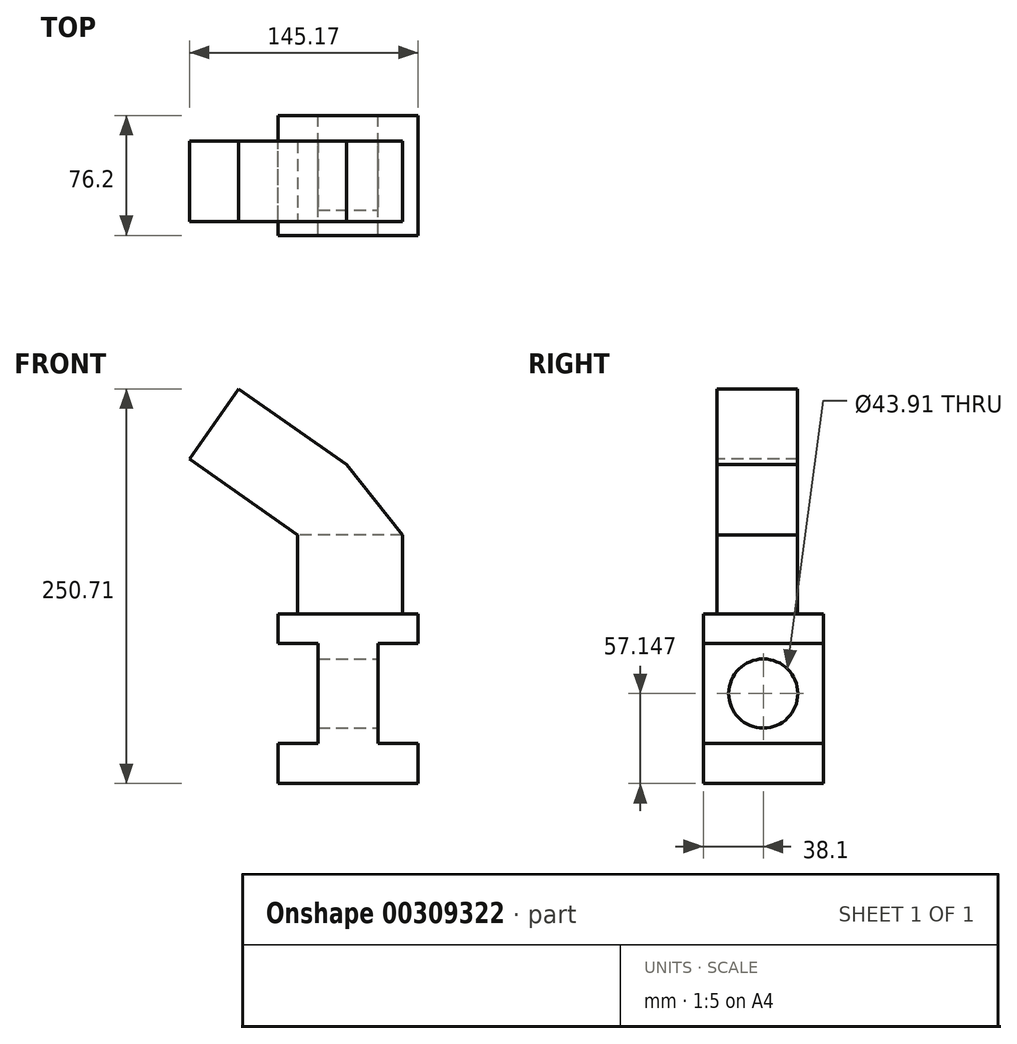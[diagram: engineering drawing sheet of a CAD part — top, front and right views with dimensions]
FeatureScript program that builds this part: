
annotation { "Feature Type Name" : "Feature", "Feature Type Description" : "" }
export const myFeature = defineFeature(function(context is Context, id is Id, definition is map)
    precondition{}
    {
        {
            var Q0;
            Q0=qCreatedBy(makeId("Front.planeOp"),FACE);
            var sketch = newSketch(context, id + "F0", { "sketchPlane" : qUnion([Q0])});
            skLineSegment(sketch, "E0", {"start": v(-43.68, -35.07) * mm, "end": v(45.22, -35.07) * mm});
            skLineSegment(sketch, "E1", {"start": v(45.22, -35.07) * mm, "end": v(45.22, -9.67) * mm});
            skLineSegment(sketch, "E2", {"start": v(45.22, -9.67) * mm, "end": v(19.82, -9.67) * mm});
            skLineSegment(sketch, "E3", {"start": v(19.82, -9.67) * mm, "end": v(19.82, 53.83) * mm});
            skLineSegment(sketch, "E4", {"start": v(19.82, 53.83) * mm, "end": v(45.22, 53.83) * mm});
            skLineSegment(sketch, "E5", {"start": v(45.22, 53.83) * mm, "end": v(45.22, 72.53) * mm});
            skLineSegment(sketch, "E6", {"start": v(45.22, 72.53) * mm, "end": v(-43.68, 72.53) * mm});
            skLineSegment(sketch, "E7", {"start": v(-43.68, 72.53) * mm, "end": v(-43.68, 53.83) * mm});
            skLineSegment(sketch, "E8", {"start": v(-43.68, 53.83) * mm, "end": v(-18.28, 53.83) * mm});
            skLineSegment(sketch, "E9", {"start": v(-18.28, 53.83) * mm, "end": v(-18.28, -9.67) * mm});
            skLineSegment(sketch, "E10", {"start": v(-18.28, -9.67) * mm, "end": v(-43.68, -9.67) * mm});
            skLineSegment(sketch, "E11", {"start": v(-43.68, -9.67) * mm, "end": v(-43.68, -35.07) * mm});
            skSolve(sketch);
        }
        {
            var Q0;
            Q0=makeQuery(id+"F0.imprint","IMPRINT",FACE,{"disambiguationData":[TD([[makeQuery(id+"F0.imprint","IMPRINT",EDGE,{"derivedFrom":sQuery(id+"F0.wireOp",EDGE,"E0")}),1.0]])]});
            extrude(context, id + "F1", {"entities" : qUnion([Q0]), "depth" : 76.2 * mm});
        }
        {
            var Q0;
            Q0=makeQuery(id+"F1.opExtrude","SWEPT_FACE",FACE,{"disambiguationData":[OSD([sQuery(id+"F0.wireOp",EDGE,"E3")])]});
            var sketch = newSketch(context, id + "F2", { "sketchPlane" : qUnion([Q0])});
            skCircle(sketch, "E12", {"center": v(-38.1, 22.08) * mm, "radius": 21.95 * mm});
            skPoint(sketch, "E12.centerSnap0", {"position": v(-38.1, 53.83) * mm});
            skPoint(sketch, "E12.centerSnap1", {"position": v(-76.2, 22.08) * mm});
            skSolve(sketch);
        }
        {
            var Q0;
            Q0=makeQuery(id+"F2.imprint","IMPRINT",FACE,{"disambiguationData":[TD([[makeQuery(id+"F2.imprint","IMPRINT",EDGE,{"derivedFrom":sQuery(id+"F2.wireOp",EDGE,"E12")}),1.0]])]});
            extrude(context, id + "F3", {"entities" : qUnion([Q0]), "operationType" : NewBodyOperationType.REMOVE, "endBound" : BoundingType.THROUGH_ALL, "oppositeDirection" : true, "depth" : 25.4 * mm});
        }
        {
            var Q0;
            Q0=makeQuery(id+"F1.opExtrude","SWEPT_FACE",FACE,{"disambiguationData":[OSD([sQuery(id+"F0.wireOp",EDGE,"E6")])]});
            var sketch = newSketch(context, id + "F4", { "sketchPlane" : qUnion([Q0])});
            skLineSegment(sketch, "E13", {"start": v(35.27, -16.41) * mm, "end": v(-31.35, -16.41) * mm});
            skLineSegment(sketch, "E14", {"start": v(-31.35, -16.41) * mm, "end": v(-31.35, -67.35) * mm});
            skLineSegment(sketch, "E15", {"start": v(-31.35, -67.35) * mm, "end": v(35.27, -67.35) * mm});
            skLineSegment(sketch, "E16", {"start": v(35.27, -67.35) * mm, "end": v(35.27, -16.41) * mm});
            skSolve(sketch);
        }
        {
            var Q0;
            Q0=makeQuery(id+"F4.imprint","IMPRINT",FACE,{"disambiguationData":[TD([[makeQuery(id+"F4.imprint","IMPRINT",EDGE,{"derivedFrom":sQuery(id+"F4.wireOp",EDGE,"E13")}),1.0]])]});
            extrude(context, id + "F5", {"entities" : qUnion([Q0]), "operationType" : NewBodyOperationType.ADD, "depth" : 50.3 * mm});
        }
        {
            var Q0;
            Q0=makeQuery(id+"F5.opExtrude","SWEPT_FACE",FACE,{"disambiguationData":[OSD([sQuery(id+"F4.wireOp",EDGE,"E15")])]});
            var sketch = newSketch(context, id + "F6", { "sketchPlane" : qUnion([Q0])});
            skLineSegment(sketch, "E17", {"start": v(-31.35, 122.82) * mm, "end": v(0, 167.47) * mm});
            skLineSegment(sketch, "E18", {"start": v(0, 167.47) * mm, "end": v(35.27, 122.82) * mm});
            skSolve(sketch);
        }
        {
            var Q0;
            Q0=makeQuery(id+"F6.imprint","IMPRINT",FACE,{"disambiguationData":[TD([[makeQuery(id+"F6.imprint","IMPRINT",EDGE,{"derivedFrom":sQuery(id+"F6.wireOp",EDGE,"E17")}),-1.0]])]});
            extrude(context, id + "F7", {"entities" : qUnion([Q0]), "operationType" : NewBodyOperationType.ADD, "oppositeDirection" : true, "depth" : 51.05 * mm});
        }
        {
            var Q0;
            {var subQ0=sQuery(id+"F4.wireOp",EDGE,"E15");Q0=makeQuery(id+"F7.boolean.opBoolean","MERGE",FACE,{"derivedFrom":[makeQuery(id+"F5.opExtrude","SWEPT_FACE",FACE,{"disambiguationData":[OSD([subQ0])]}),makeQuery(id+"F7.opExtrude","CAP_FACE",FACE,{"disambiguationData":[OSD([subQ0,sQuery(id+"F6.wireOp",EDGE,"E17"),sQuery(id+"F6.wireOp",EDGE,"E18")])],"isStart":true})]});}
            var sketch = newSketch(context, id + "F8", { "sketchPlane" : qUnion([Q0])});
            skPoint(sketch, "E19.oppositeSnap0", {"position": v(-31.35, 97.67) * mm});
            skLineSegment(sketch, "E19.bottom", {"start": v(-31.35, 97.67) * mm, "end": v(-11.19, 97.67) * mm});
            skLineSegment(sketch, "E19.top", {"start": v(-31.35, 97.67) * mm, "end": v(-11.19, 97.67) * mm});
            skLineSegment(sketch, "E19.left", {"start": v(-31.35, 97.67) * mm, "end": v(-31.35, 97.67) * mm});
            skLineSegment(sketch, "E19.right", {"start": v(-11.19, 97.67) * mm, "end": v(-11.19, 97.67) * mm});
            skLineSegment(sketch, "E20", {"start": v(-11.19, 97.67) * mm, "end": v(-11.19, 72.53) * mm});
            skSolve(sketch);
        }
        {
            var Q0;
            Q0=makeQuery(id+"F7.opExtrude","SWEPT_FACE",FACE,{"disambiguationData":[OSD([sQuery(id+"F6.wireOp",EDGE,"E17")])]});
            extrude(context, id + "F9", {"entities" : qUnion([Q0]), "operationType" : NewBodyOperationType.ADD, "depth" : 83.82 * mm});
        }
    });
